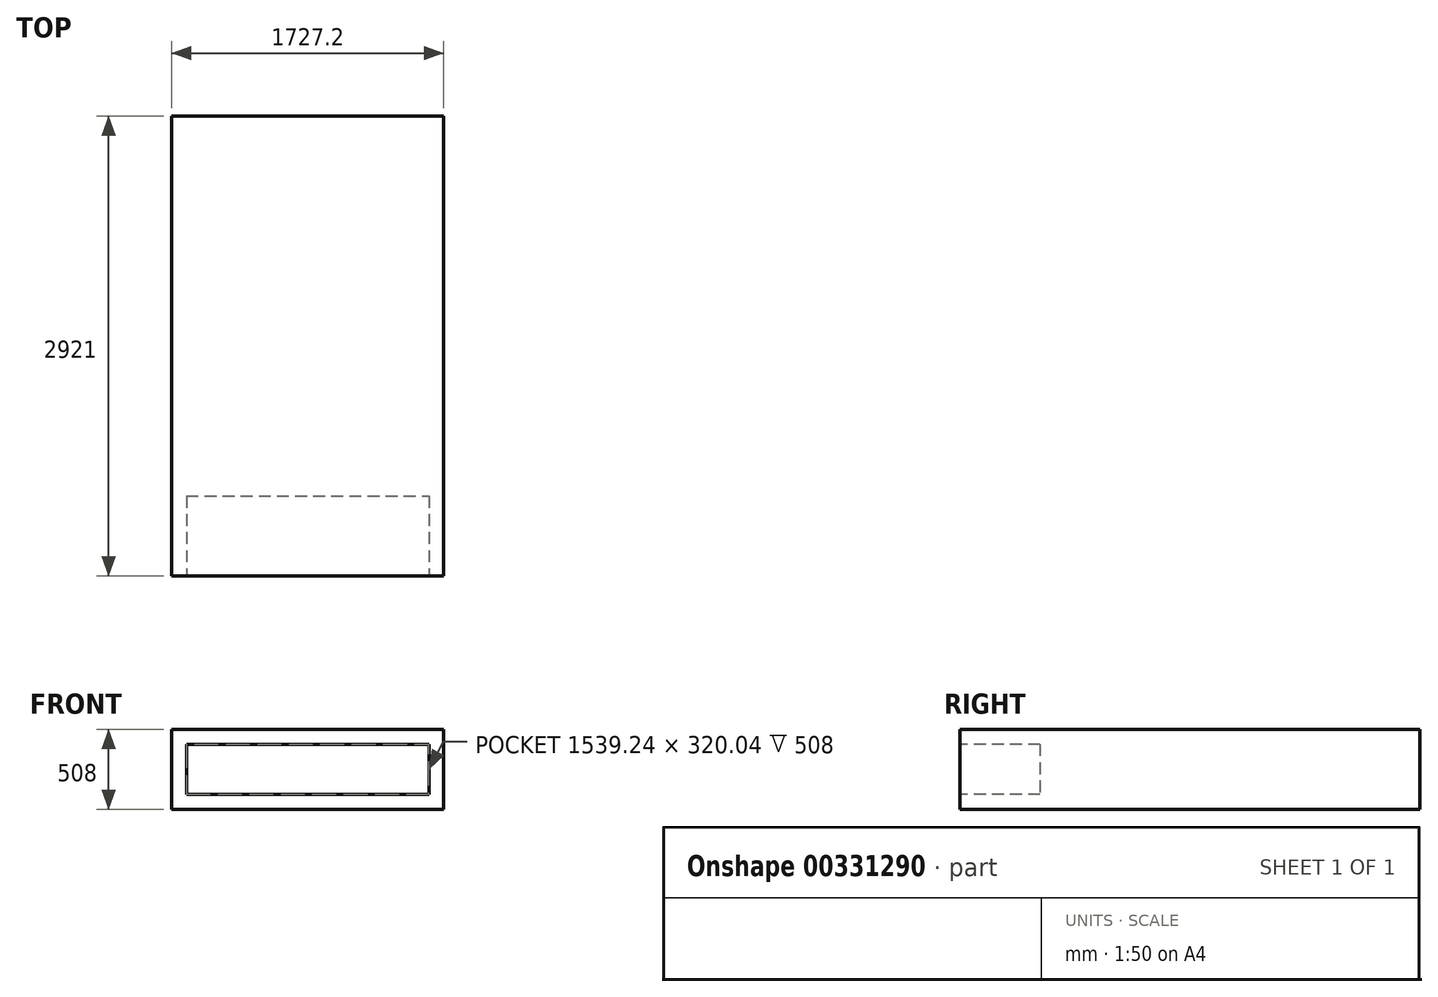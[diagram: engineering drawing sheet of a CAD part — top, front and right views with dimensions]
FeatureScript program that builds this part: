
annotation { "Feature Type Name" : "Feature", "Feature Type Description" : "" }
export const myFeature = defineFeature(function(context is Context, id is Id, definition is map)
    precondition{}
    {
        {
            var Q0;
            Q0=qCreatedBy(makeId("Top.planeOp"),FACE);
            var sketch = newSketch(context, id + "F0", { "sketchPlane" : qUnion([Q0])});
            skLineSegment(sketch, "E0.bottom", {"start": v(0, 0) * mm, "end": v(1727.2, 0) * mm});
            skLineSegment(sketch, "E0.top", {"start": v(0, 2921) * mm, "end": v(1727.2, 2921) * mm});
            skLineSegment(sketch, "E0.left", {"start": v(0, 0) * mm, "end": v(0, 2921) * mm});
            skLineSegment(sketch, "E0.right", {"start": v(1727.2, 0) * mm, "end": v(1727.2, 2921) * mm});
            skSolve(sketch);
        }
        {
            var Q0;
            Q0 = qSketchRegion(id + "F0", true);
            extrude(context, id + "F1", {"entities" : qUnion([Q0]), "depth" : 508 * mm});
        }
        {
            var Q0;
            Q0=makeQuery(id+"F1.opExtrude","SWEPT_FACE",FACE,{"disambiguationData":[OSD([sQuery(id+"F0.wireOp",EDGE,"E0.bottom")])]});
            var sketch = newSketch(context, id + "F2", { "sketchPlane" : qUnion([Q0])});
            skLineSegment(sketch, "E1.0", {"start": v(93.98, 414.02) * mm, "end": v(1633.22, 414.02) * mm});
            skLineSegment(sketch, "E1.1", {"start": v(93.98, 414.02) * mm, "end": v(93.98, 93.98) * mm});
            skLineSegment(sketch, "E1.2", {"start": v(93.98, 93.98) * mm, "end": v(1633.22, 93.98) * mm});
            skLineSegment(sketch, "E1.3", {"start": v(1633.22, 414.02) * mm, "end": v(1633.22, 93.98) * mm});
            skSolve(sketch);
        }
        {
            var Q0;
            Q0 = qSketchRegion(id + "F2", true);
            extrude(context, id + "F3", {"entities" : qUnion([Q0]), "operationType" : NewBodyOperationType.REMOVE, "oppositeDirection" : true, "depth" : 508 * mm});
        }
    });
